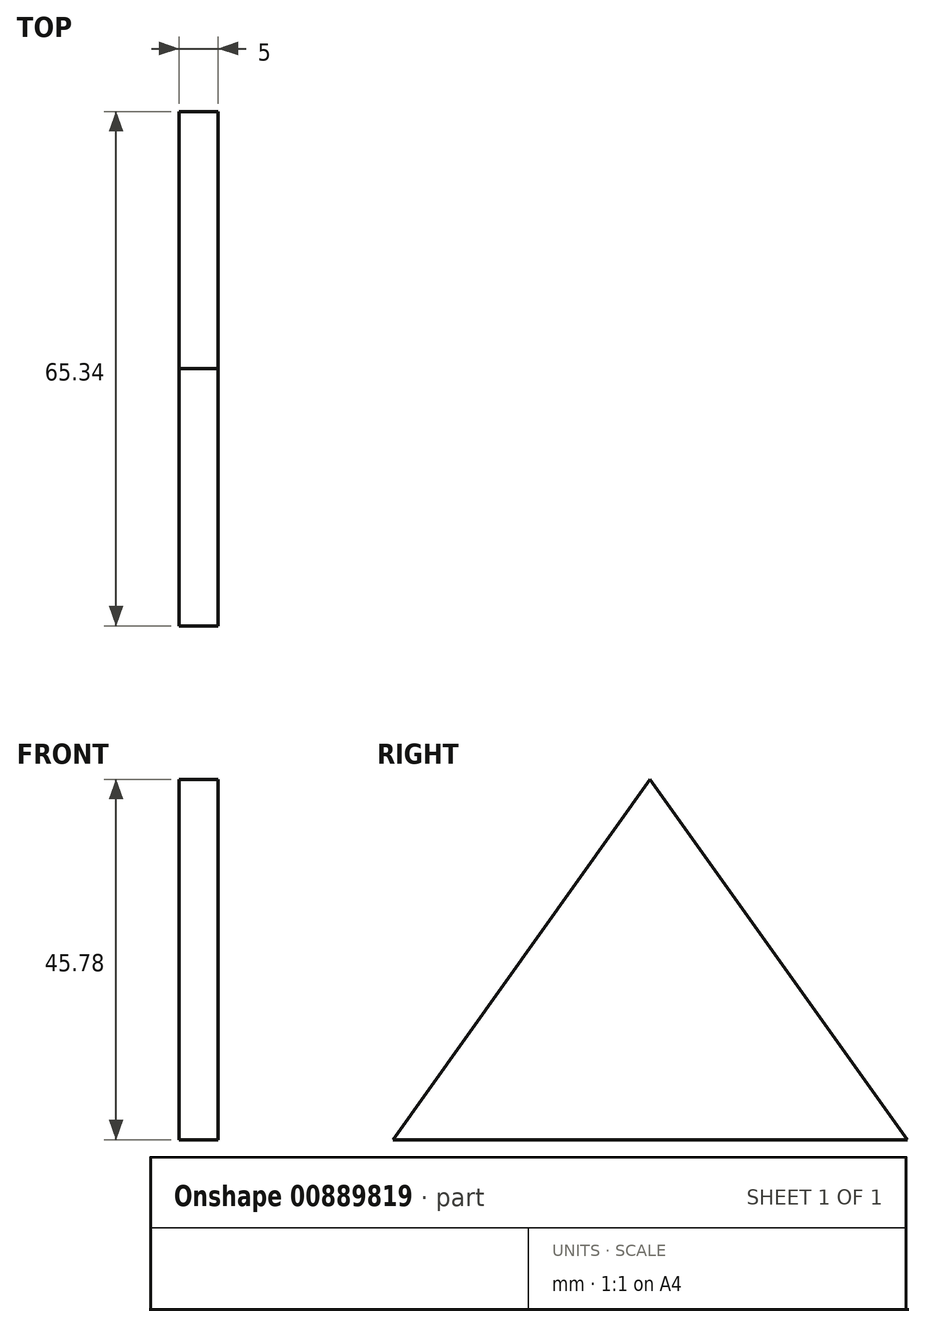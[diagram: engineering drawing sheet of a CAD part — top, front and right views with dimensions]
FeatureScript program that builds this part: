
annotation { "Feature Type Name" : "Feature", "Feature Type Description" : "" }
export const myFeature = defineFeature(function(context is Context, id is Id, definition is map)
    precondition{}
    {
        {
            var Q0;
            Q0=qCreatedBy(makeId("Top.planeOp"),FACE);
            var sketch = newSketch(context, id + "F0", { "sketchPlane" : qUnion([Q0])});
            skCircle(sketch, "E0", {"center": v(0, 0) * mm, "radius": 7.5 * mm});
            skSolve(sketch);
        }
        {
            var Q0;
            Q0=sQuery(id+"F0.wireOp",EDGE,"E0");
            extrude(context, id + "F1", {"bodyType" : ToolBodyType.SURFACE, "surfaceEntities" : qUnion([Q0]), "depth" : 40 * mm, "offsetDistance" : 25.4 * mm});
        }
        {
            var Q0;
            Q0=qCreatedBy(makeId("Right.planeOp"),FACE);
            var sketch = newSketch(context, id + "F2", { "sketchPlane" : qUnion([Q0])});
            skLineSegment(sketch, "E1", {"start": v(0, 0) * mm, "end": v(0, 50.07) * mm});
            skLineSegment(sketch, "E2", {"start": v(0, 50.07) * mm, "end": v(-32.67, 4.29) * mm});
            skLineSegment(sketch, "E3", {"start": v(-32.67, 4.29) * mm, "end": v(0, 4.29) * mm});
            skLineSegment(sketch, "E4.MirrorCS", {"start": v(0, 50.07) * mm, "end": v(32.67, 4.29) * mm});
            skLineSegment(sketch, "E5.MirrorCS", {"start": v(32.67, 4.29) * mm, "end": v(0, 4.29) * mm});
            skSolve(sketch);
        }
        {
            var Q0;
            Q0 = qSketchRegion(id + "F2", true);
            extrude(context, id + "F3", {"entities" : qUnion([Q0]), "depth" : 5 * mm, "offsetDistance" : 25.4 * mm});
        }
    });
